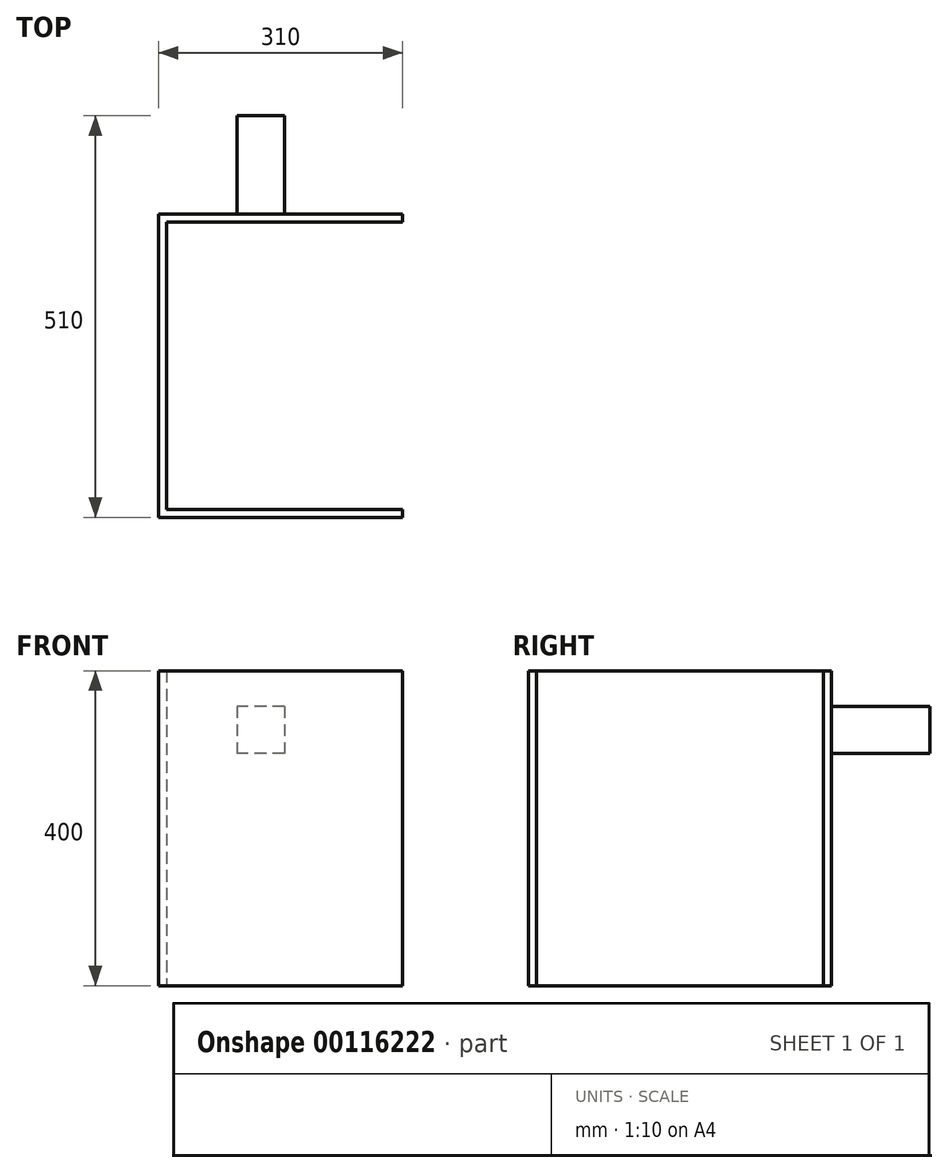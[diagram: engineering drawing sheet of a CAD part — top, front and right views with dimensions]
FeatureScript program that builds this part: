
annotation { "Feature Type Name" : "Feature", "Feature Type Description" : "" }
export const myFeature = defineFeature(function(context is Context, id is Id, definition is map)
    precondition{}
    {
        {
            var Q0;
            Q0=qCreatedBy(makeId("Top.planeOp"),FACE);
            var sketch = newSketch(context, id + "F0", { "sketchPlane" : qUnion([Q0])});
            skLineSegment(sketch, "E0", {"start": v(0, 0) * mm, "end": v(0, 385) * mm});
            skLineSegment(sketch, "E1", {"start": v(0, 385) * mm, "end": v(310, 385) * mm});
            skLineSegment(sketch, "E2", {"start": v(0, 0) * mm, "end": v(310, 0) * mm});
            skLineSegment(sketch, "E3.0", {"start": v(10, 375) * mm, "end": v(310, 375) * mm});
            skLineSegment(sketch, "E3.1", {"start": v(10, 10) * mm, "end": v(10, 375) * mm});
            skLineSegment(sketch, "E3.2", {"start": v(10, 10) * mm, "end": v(310, 10) * mm});
            skLineSegment(sketch, "E4", {"start": v(310, 385) * mm, "end": v(310, 375) * mm});
            skLineSegment(sketch, "E5", {"start": v(310, 10) * mm, "end": v(310, 0) * mm});
            skSolve(sketch);
        }
        {
            var Q0;
            Q0 = qSketchRegion(id + "F0", true);
            extrude(context, id + "F1", {"entities" : qUnion([Q0]), "depth" : 400 * mm});
        }
        {
            var Q0;
            Q0=makeQuery(id+"F1.opExtrude","SWEPT_FACE",FACE,{"disambiguationData":[OSD([sQuery(id+"F0.wireOp",EDGE,"E1")])]});
            var sketch = newSketch(context, id + "F2", { "sketchPlane" : qUnion([Q0])});
            skLineSegment(sketch, "E6.bottom", {"start": v(-160, 355) * mm, "end": v(-100, 355) * mm});
            skLineSegment(sketch, "E6.top", {"start": v(-160, 295) * mm, "end": v(-100, 295) * mm});
            skLineSegment(sketch, "E6.left", {"start": v(-160, 355) * mm, "end": v(-160, 295) * mm});
            skLineSegment(sketch, "E6.right", {"start": v(-100, 355) * mm, "end": v(-100, 295) * mm});
            skSolve(sketch);
        }
        {
            var Q0;
            Q0 = qSketchRegion(id + "F2", true);
            extrude(context, id + "F3", {"entities" : qUnion([Q0]), "operationType" : NewBodyOperationType.ADD, "depth" : 25 * mm});
        }
        {
            var Q0;
            Q0=makeQuery(id+"F3.opExtrude","CAP_FACE",FACE,{"disambiguationData":[OSD([sQuery(id+"F2.wireOp",EDGE,"E6.bottom"),sQuery(id+"F2.wireOp",EDGE,"E6.top"),sQuery(id+"F2.wireOp",EDGE,"E6.left"),sQuery(id+"F2.wireOp",EDGE,"E6.right")])],"isStart":false});
            extrude(context, id + "F4", {"entities" : qUnion([Q0]), "operationType" : NewBodyOperationType.ADD, "depth" : 100 * mm});
        }
    });
